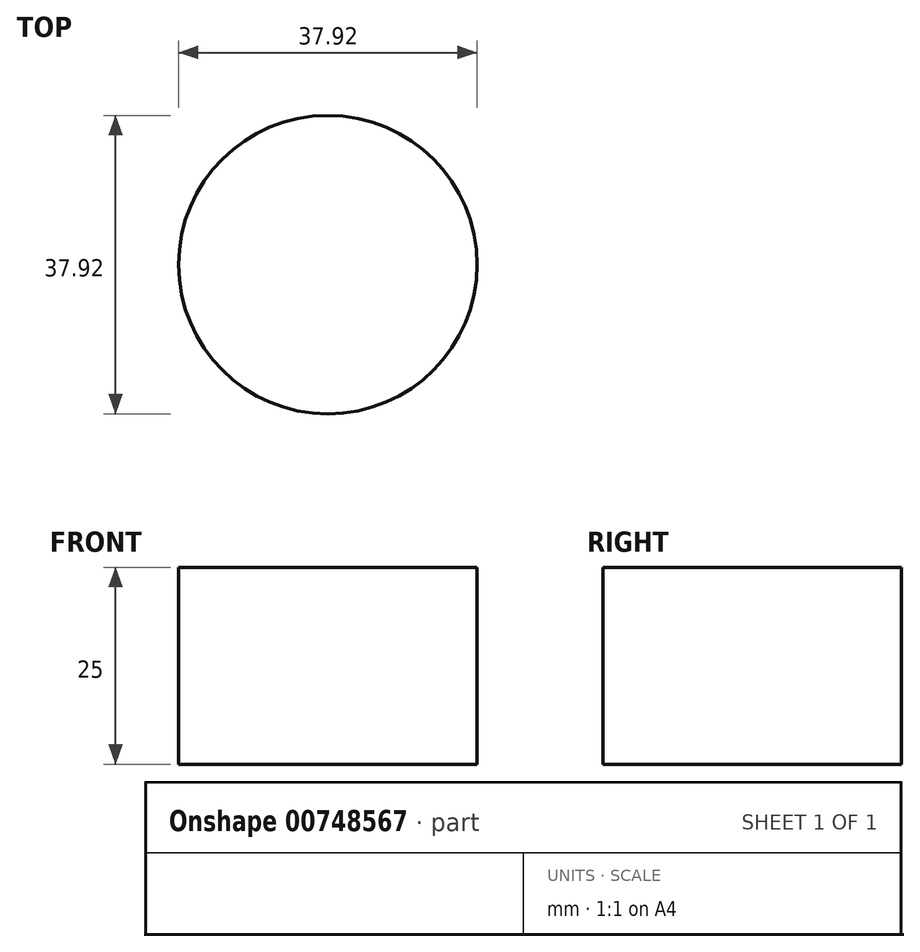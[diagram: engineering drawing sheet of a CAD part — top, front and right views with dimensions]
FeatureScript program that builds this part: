
annotation { "Feature Type Name" : "Feature", "Feature Type Description" : "" }
export const myFeature = defineFeature(function(context is Context, id is Id, definition is map)
    precondition{}
    {
        {
            var Q0;
            Q0=qCreatedBy(makeId("Top.planeOp"),FACE);
            var sketch = newSketch(context, id + "F0", { "sketchPlane" : qUnion([Q0])});
            skCircle(sketch, "E0", {"center": v(0, 0) * mm, "radius": 18.96 * mm});
            skSolve(sketch);
        }
        {
            var Q0;
            Q0=sQuery(id+"F0.wireOp",EDGE,"E0");
            extrude(context, id + "F1", {"bodyType" : ToolBodyType.SURFACE, "surfaceEntities" : qUnion([Q0]), "depth" : 25 * mm, "offsetDistance" : 25 * mm});
        }
    });
